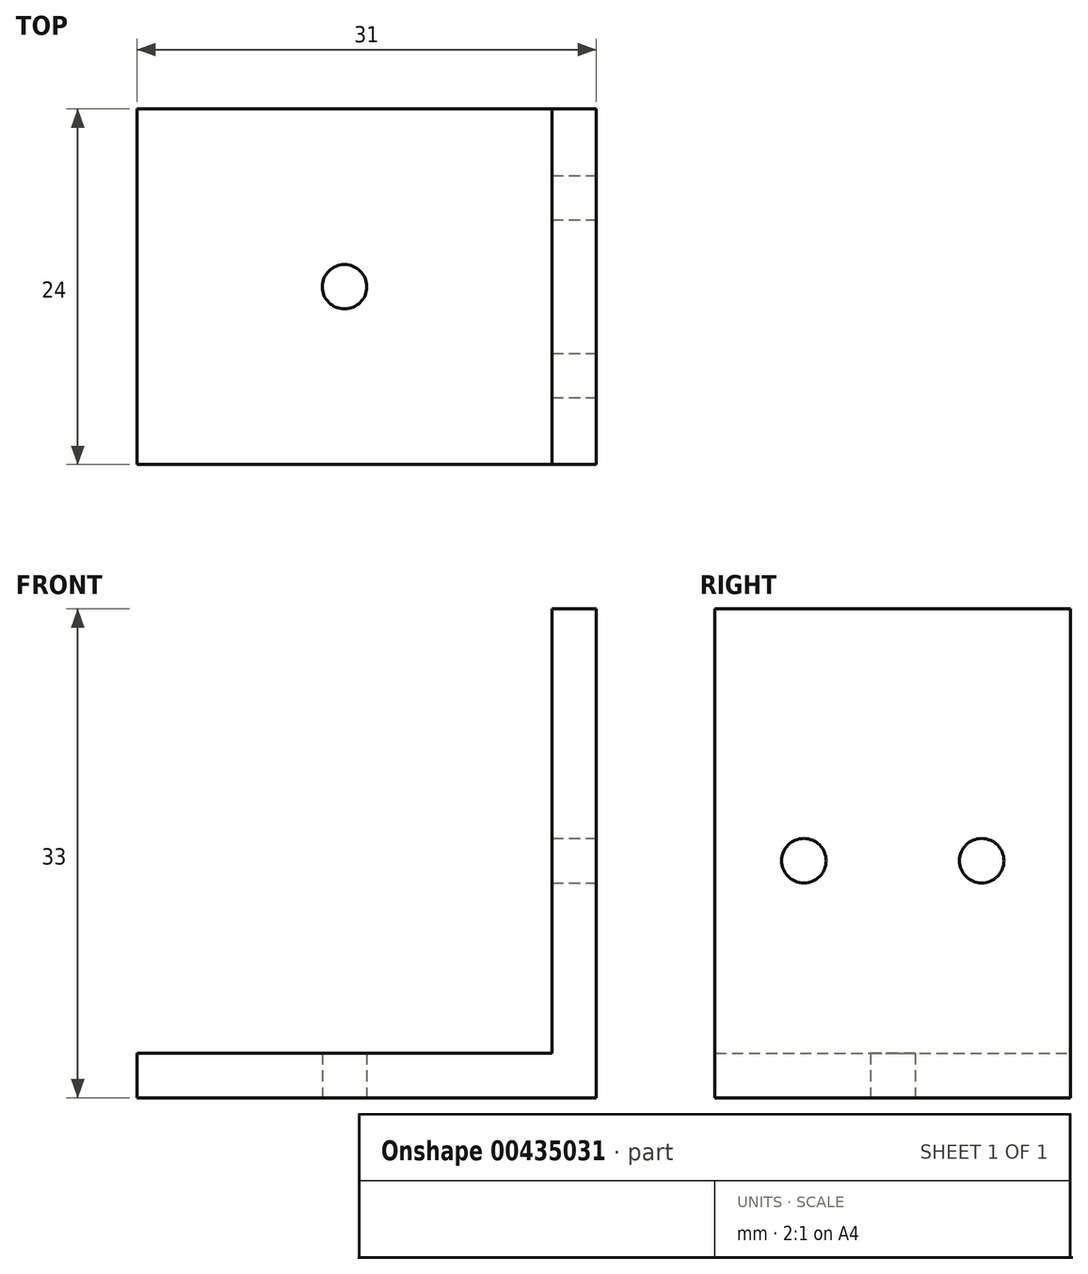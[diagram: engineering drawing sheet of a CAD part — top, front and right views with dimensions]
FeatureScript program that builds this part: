
annotation { "Feature Type Name" : "Feature", "Feature Type Description" : "" }
export const myFeature = defineFeature(function(context is Context, id is Id, definition is map)
    precondition{}
    {
        {
            var Q0;
            Q0=qCreatedBy(makeId("Top.planeOp"),FACE);
            var sketch = newSketch(context, id + "F0", { "sketchPlane" : qUnion([Q0])});
            skLineSegment(sketch, "E0.bottom", {"start": v(0, 0) * mm, "end": v(17, 0) * mm});
            skLineSegment(sketch, "E0.top", {"start": v(0, 24) * mm, "end": v(17, 24) * mm});
            skLineSegment(sketch, "E0.right", {"start": v(17, 0) * mm, "end": v(17, 24) * mm});
            skLineSegment(sketch, "E1", {"start": v(0, 0) * mm, "end": v(14, 0) * mm, "construction": true});
            skLineSegment(sketch, "E2", {"start": v(14, 0) * mm, "end": v(14, 24) * mm, "construction": true});
            skLineSegment(sketch, "E3", {"start": v(0, 12) * mm, "end": v(14, 12) * mm, "construction": true});
            skLineSegment(sketch, "E4.bottom", {"start": v(0, 0) * mm, "end": v(-14, 0) * mm});
            skLineSegment(sketch, "E4.top", {"start": v(0, 24) * mm, "end": v(-14, 24) * mm});
            skLineSegment(sketch, "E4.right", {"start": v(-14, 0) * mm, "end": v(-14, 24) * mm});
            skCircle(sketch, "E5", {"center": v(0, 12) * mm, "radius": 1.5 * mm});
            skSolve(sketch);
        }
        {
            var Q0;
            Q0 = qSketchRegion(id + "F0", true);
            extrude(context, id + "F1", {"entities" : qUnion([Q0]), "depth" : 3 * mm});
        }
        {
            var Q0;
            Q0=makeQuery(id+"F1.opExtrude","CAP_FACE",FACE,{"disambiguationData":[OSD([sQuery(id+"F0.wireOp",EDGE,"E0.bottom"),sQuery(id+"F0.wireOp",EDGE,"E0.top"),sQuery(id+"F0.wireOp",EDGE,"E0.right"),sQuery(id+"F0.wireOp",EDGE,"E4.bottom"),sQuery(id+"F0.wireOp",EDGE,"E4.top"),sQuery(id+"F0.wireOp",EDGE,"E4.right"),sQuery(id+"F0.wireOp",EDGE,"E5")])],"isStart":false});
            var sketch = newSketch(context, id + "F2", { "sketchPlane" : qUnion([Q0])});
            skLineSegment(sketch, "E6.bottom", {"start": v(17, 24) * mm, "end": v(14, 24) * mm});
            skLineSegment(sketch, "E6.top", {"start": v(17, 0) * mm, "end": v(14, 0) * mm});
            skLineSegment(sketch, "E6.left", {"start": v(17, 24) * mm, "end": v(17, 0) * mm});
            skLineSegment(sketch, "E6.right", {"start": v(14, 24) * mm, "end": v(14, 0) * mm});
            skSolve(sketch);
        }
        {
            var Q0;
            Q0=makeQuery(id+"F2.imprint","IMPRINT",FACE,{"disambiguationData":[TD([[makeQuery(id+"F2.imprint","IMPRINT",EDGE,{"derivedFrom":sQuery(id+"F2.wireOp",EDGE,"E6.bottom")}),-1.0]])]});
            extrude(context, id + "F3", {"entities" : qUnion([Q0]), "operationType" : NewBodyOperationType.ADD, "depth" : 30 * mm});
        }
        {
            var Q0;
            Q0=makeQuery(id+"F3.boolean.opBoolean","MERGE",FACE,{"derivedFrom":[makeQuery(id+"F1.opExtrude","SWEPT_FACE",FACE,{"disambiguationData":[OSD([sQuery(id+"F0.wireOp",EDGE,"E0.right")])]}),makeQuery(id+"F3.opExtrude","SWEPT_FACE",FACE,{"disambiguationData":[OSD([sQuery(id+"F2.wireOp",EDGE,"E6.left")])]})]});
            var sketch = newSketch(context, id + "F4", { "sketchPlane" : qUnion([Q0])});
            skLineSegment(sketch, "E7", {"start": v(24, 33) * mm, "end": v(24, 16) * mm, "construction": true});
            skLineSegment(sketch, "E8", {"start": v(24, 16) * mm, "end": v(0, 16) * mm, "construction": true});
            skLineSegment(sketch, "E9", {"start": v(0, 16) * mm, "end": v(6, 16) * mm, "construction": true});
            skLineSegment(sketch, "E10", {"start": v(6, 16) * mm, "end": v(18, 16) * mm, "construction": true});
            skCircle(sketch, "E11", {"center": v(18, 16) * mm, "radius": 1.5 * mm});
            skCircle(sketch, "E12", {"center": v(6, 16) * mm, "radius": 1.5 * mm});
            skLineSegment(sketch, "E13", {"start": v(24, 16) * mm, "end": v(24, 0) * mm, "construction": true});
            skSolve(sketch);
        }
        {
            var Q0;
            Q0=makeQuery(id+"F4.imprint","IMPRINT",FACE,{"disambiguationData":[TD([[makeQuery(id+"F4.imprint","IMPRINT",EDGE,{"derivedFrom":sQuery(id+"F4.wireOp",EDGE,"E12")}),1.0]])]});
            var Q1;
            Q1=makeQuery(id+"F4.imprint","IMPRINT",FACE,{"disambiguationData":[TD([[makeQuery(id+"F4.imprint","IMPRINT",EDGE,{"derivedFrom":sQuery(id+"F4.wireOp",EDGE,"E11")}),1.0]])]});
            extrude(context, id + "F5", {"entities" : qUnion([Q0, Q1]), "operationType" : NewBodyOperationType.REMOVE, "oppositeDirection" : true, "depth" : 25 * mm});
        }
    });
